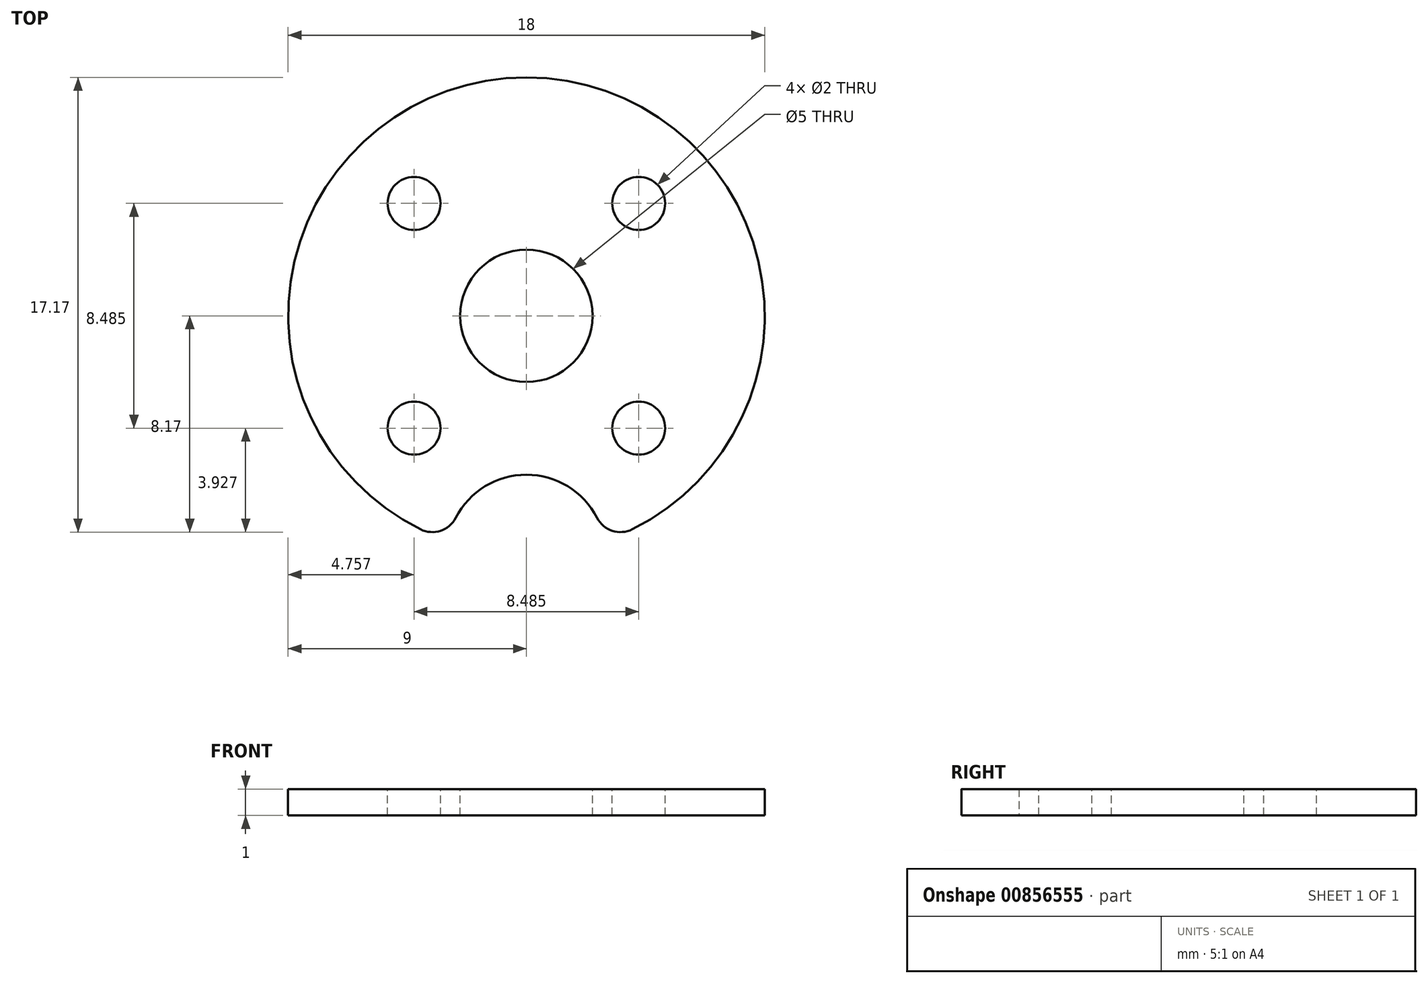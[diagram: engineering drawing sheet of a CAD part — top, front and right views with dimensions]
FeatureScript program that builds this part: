
annotation { "Feature Type Name" : "Feature", "Feature Type Description" : "" }
export const myFeature = defineFeature(function(context is Context, id is Id, definition is map)
    precondition{}
    {
        {
            var Q0;
            Q0=qCreatedBy(makeId("Top.planeOp"),FACE);
            var sketch = newSketch(context, id + "F0", { "sketchPlane" : qUnion([Q0])});
            skCircle(sketch, "E0", {"center": v(0, 0) * mm, "radius": 6 * mm, "construction": true});
            skLineSegment(sketch, "E1.bottom", {"start": v(4.24, 4.24) * mm, "end": v(-4.24, 4.24) * mm, "construction": true});
            skLineSegment(sketch, "E1.top", {"start": v(4.24, -4.24) * mm, "end": v(-4.24, -4.24) * mm, "construction": true});
            skLineSegment(sketch, "E1.left", {"start": v(4.24, 4.24) * mm, "end": v(4.24, -4.24) * mm, "construction": true});
            skLineSegment(sketch, "E1.right", {"start": v(-4.24, 4.24) * mm, "end": v(-4.24, -4.24) * mm, "construction": true});
            skCircle(sketch, "E2", {"center": v(0, 0) * mm, "radius": 2.5 * mm, "construction": true});
            skCircle(sketch, "E3", {"center": v(4.24, 4.24) * mm, "radius": 1 * mm, "construction": true});
            skCircle(sketch, "E4.0", {"center": v(0, 0) * mm, "radius": 2.5 * mm});
            skCircle(sketch, "E5.0", {"center": v(4.24, 4.24) * mm, "radius": 1 * mm});
            skCircle(sketch, "E6", {"center": v(0, 0) * mm, "radius": 9 * mm});
            skCircle(sketch, "E7.1.0", {"center": v(-4.24, 4.24) * mm, "radius": 1 * mm});
            skCircle(sketch, "E7.2.0", {"center": v(-4.24, -4.24) * mm, "radius": 1 * mm});
            skCircle(sketch, "E7.3.0", {"center": v(4.24, -4.24) * mm, "radius": 1 * mm});
            skSolve(sketch);
        }
        {
            var Q0;
            Q0=qCreatedBy(makeId("Front.planeOp"),FACE);
            var sketch = newSketch(context, id + "F1", { "sketchPlane" : qUnion([Q0])});
            skLineSegment(sketch, "E8", {"start": v(0, 0) * mm, "end": v(0, 1) * mm});
            skSolve(sketch);
        }
        {
            var Q0;
            Q0=qCreatedBy(makeId("Top.planeOp"),FACE);
            var sketch = newSketch(context, id + "F2", { "sketchPlane" : qUnion([Q0])});
            skCircle(sketch, "E9.0", {"center": v(0, 0) * mm, "radius": 9 * mm, "construction": true});
            skCircle(sketch, "E10", {"center": v(0, -9) * mm, "radius": 3 * mm});
            skSolve(sketch);
        }
        {
            var Q0;
            Q0=qSketchRegion(id+"F0",true);
            var Q1;
            Q1=sQuery(id+"F1.wireOp",EDGE,"E8");
            sweep(context, id + "F3", {"profiles" : qUnion([Q0]), "path" : qUnion([Q1])});
        }
        {
            var Q0;
            Q0=qSketchRegion(id+"F2",true);
            extrude(context, id + "F4", {"entities" : qUnion([Q0]), "operationType" : NewBodyOperationType.REMOVE, "endBound" : BoundingType.THROUGH_ALL, "depth" : 25 * mm, "offsetDistance" : 25 * mm});
        }
        {
            var Q0;
            Q0=makeQuery(id+"F4.boolean.opBoolean","INTERSECT",EDGE,{"disambiguationData":[OD(1.0)],"derivedFrom":[makeQuery(id+"F3.opSweep","SWEPT_FACE",FACE,{"disambiguationData":[OSD([sQuery(id+"F0.wireOp",EDGE,"E6"),sQuery(id+"F1.wireOp",EDGE,"E8")])]}),makeQuery(id+"F4.opExtrude","SWEPT_FACE",FACE,{"disambiguationData":[OSD([sQuery(id+"F2.wireOp",EDGE,"E10")])]})]});
            var Q1;
            Q1=makeQuery(id+"F4.boolean.opBoolean","INTERSECT",EDGE,{"disambiguationData":[OD(0.0)],"derivedFrom":[makeQuery(id+"F3.opSweep","SWEPT_FACE",FACE,{"disambiguationData":[OSD([sQuery(id+"F0.wireOp",EDGE,"E6"),sQuery(id+"F1.wireOp",EDGE,"E8")])]}),makeQuery(id+"F4.opExtrude","SWEPT_FACE",FACE,{"disambiguationData":[OSD([sQuery(id+"F2.wireOp",EDGE,"E10")])]})]});
            fillet(context, id + "F5", {"entities" : qUnion([Q0, Q1]), "radius" : 1 * mm, "tangentPropagation" : true, "allowEdgeOverflow" : false});
        }
    });
